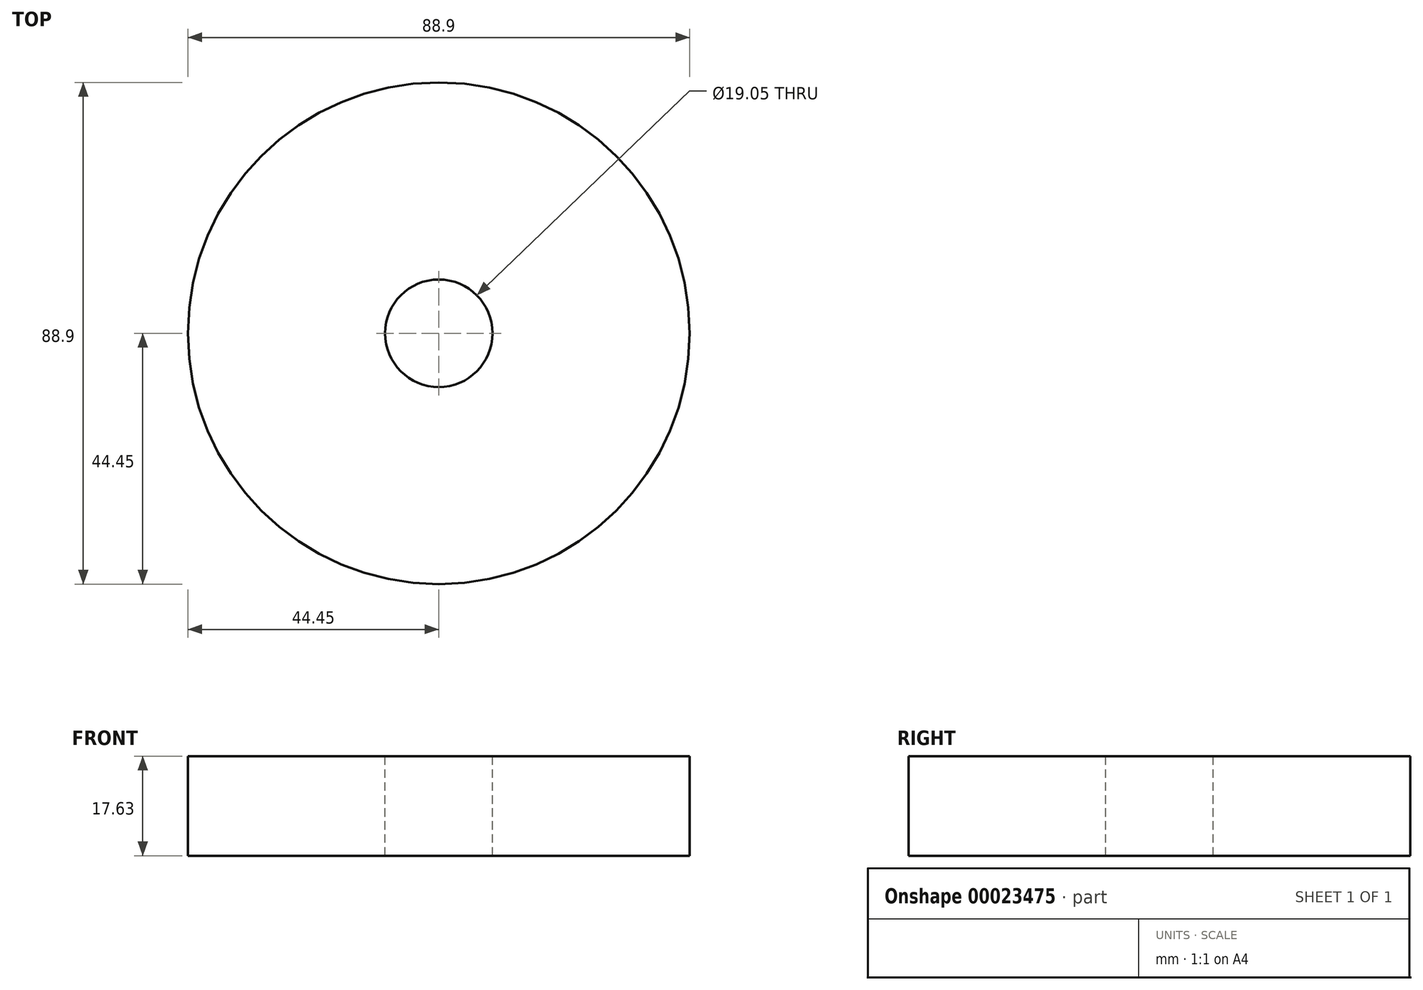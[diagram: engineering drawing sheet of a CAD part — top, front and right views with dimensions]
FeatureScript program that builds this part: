
annotation { "Feature Type Name" : "Feature", "Feature Type Description" : "" }
export const myFeature = defineFeature(function(context is Context, id is Id, definition is map)
    precondition{}
    {
        {
            var Q0;
            Q0=qCreatedBy(makeId("Front.planeOp"),FACE);
            var sketch = newSketch(context, id + "F0", { "sketchPlane" : qUnion([Q0])});
            skLineSegment(sketch, "E0", {"start": v(0, 27.77) * mm, "end": v(0, -28.95) * mm, "construction": true});
            skLineSegment(sketch, "E1.bottom", {"start": v(9.52, -28.95) * mm, "end": v(44.45, -28.95) * mm});
            skLineSegment(sketch, "E1.top", {"start": v(9.52, -11.32) * mm, "end": v(44.45, -11.32) * mm});
            skLineSegment(sketch, "E1.right", {"start": v(44.45, -28.95) * mm, "end": v(44.45, -11.32) * mm});
            skLineSegment(sketch, "E2.bottom", {"start": v(9.52, -11.32) * mm, "end": v(25.4, -11.32) * mm});
            skLineSegment(sketch, "E2.top", {"start": v(9.52, 45.83) * mm, "end": v(25.4, 45.83) * mm});
            skLineSegment(sketch, "E2.right", {"start": v(25.4, -11.32) * mm, "end": v(25.4, 45.83) * mm});
            skLineSegment(sketch, "E3.bottom", {"start": v(9.52, 45.83) * mm, "end": v(19.05, 45.83) * mm});
            skLineSegment(sketch, "E3.top", {"start": v(9.52, 58.53) * mm, "end": v(19.05, 58.53) * mm});
            skLineSegment(sketch, "E3.right", {"start": v(19.05, 45.83) * mm, "end": v(19.05, 58.53) * mm});
            skLineSegment(sketch, "E4", {"start": v(9.52, 58.53) * mm, "end": v(9.52, -28.95) * mm});
            skSolve(sketch);
        }
        {
            var Q0;
            {var subQ2=sQuery(id+"F0.wireOp",EDGE,"E3.bottom");Q0=makeQuery(id+"F0.imprint","IMPRINT",FACE,{"disambiguationData":[TD([[makeQuery(id+"F0.imprint","IMPRINT",EDGE,{"derivedFrom":subQ2}),1.0]])]});}
            var Q1;
            {var subQ2=sQuery(id+"F0.wireOp",EDGE,"E2.bottom");Q1=makeQuery(id+"F0.imprint","IMPRINT",FACE,{"disambiguationData":[TD([[makeQuery(id+"F0.imprint","IMPRINT",EDGE,{"derivedFrom":subQ2}),1.0]])]});}
            var Q2;
            {var subQ2=sQuery(id+"F0.wireOp",EDGE,"E1.bottom");Q2=makeQuery(id+"F0.imprint","IMPRINT",FACE,{"disambiguationData":[TD([[makeQuery(id+"F0.imprint","IMPRINT",EDGE,{"derivedFrom":subQ2}),1.0]])]});}
            var Q3;
            Q3=sQuery(id+"F0.wireOp",EDGE,"E0");
            revolve(context, id + "F1", {"entities" : qUnion([Q0, Q1, Q2]), "axis" : qUnion([Q3]), "revolveType" : RevolveType.FULL});
        }
    });
